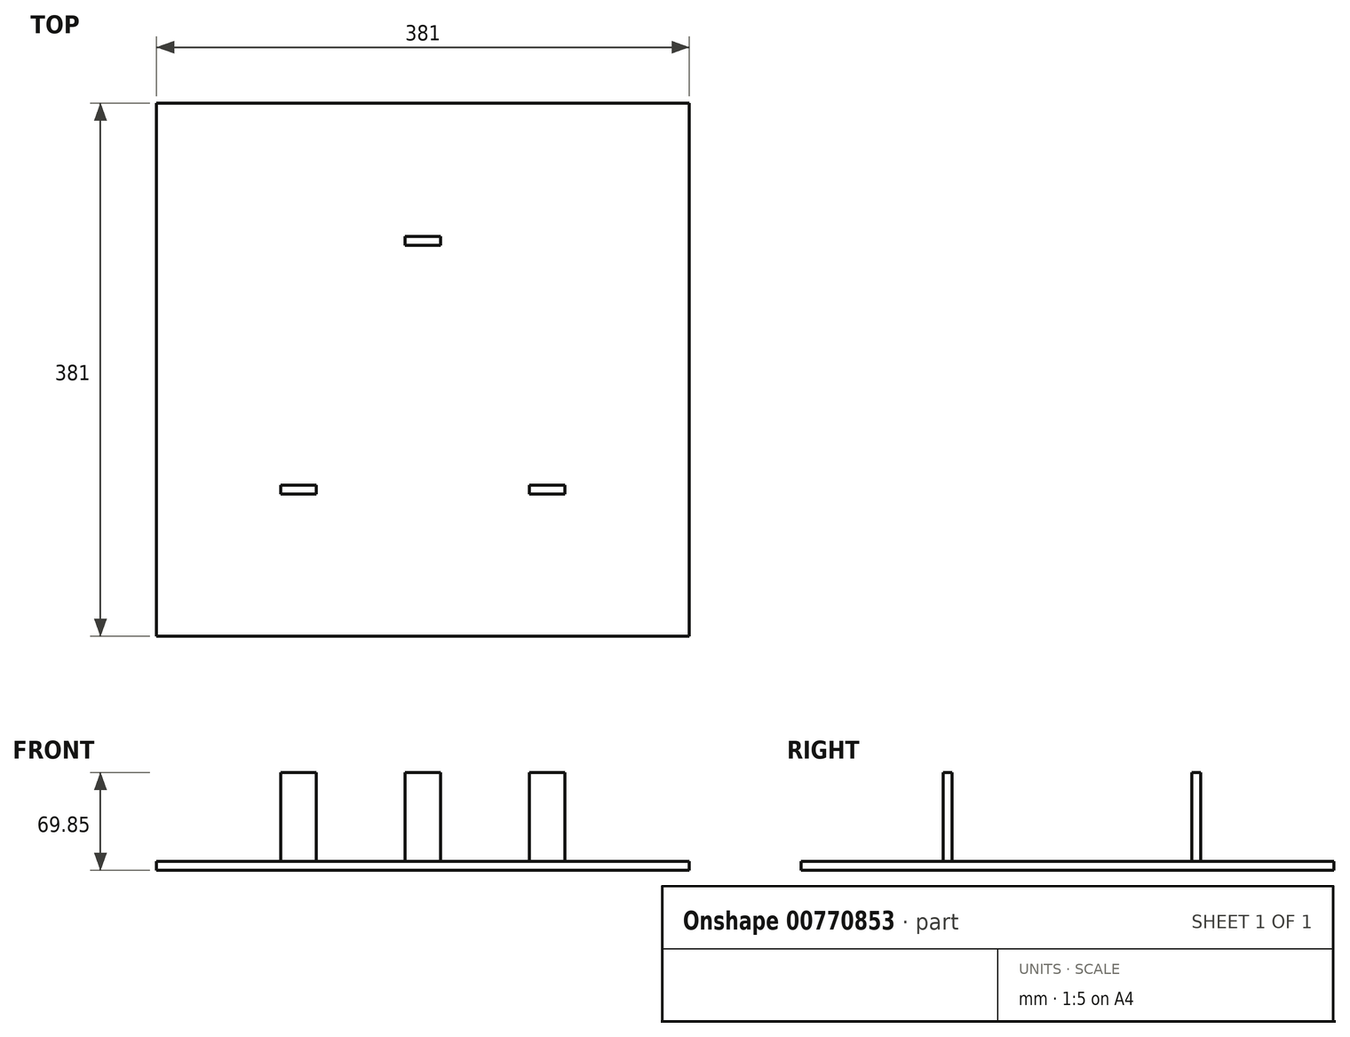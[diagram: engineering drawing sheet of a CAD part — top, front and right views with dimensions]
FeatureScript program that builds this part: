
annotation { "Feature Type Name" : "Feature", "Feature Type Description" : "" }
export const myFeature = defineFeature(function(context is Context, id is Id, definition is map)
    precondition{}
    {
        {
            var Q0;
            Q0=qCreatedBy(makeId("Top.planeOp"),FACE);
            var sketch = newSketch(context, id + "F0", { "sketchPlane" : qUnion([Q0])});
            skLineSegment(sketch, "E0.bottom", {"start": v(-202.72, 255.29) * mm, "end": v(178.28, 255.29) * mm});
            skLineSegment(sketch, "E0.top", {"start": v(-202.72, -125.71) * mm, "end": v(178.28, -125.71) * mm});
            skLineSegment(sketch, "E0.left", {"start": v(-202.72, 255.29) * mm, "end": v(-202.72, -125.71) * mm});
            skLineSegment(sketch, "E0.right", {"start": v(178.28, 255.29) * mm, "end": v(178.28, -125.71) * mm});
            skSolve(sketch);
        }
        {
            var Q0;
            Q0 = qSketchRegion(id + "F0", true);
            extrude(context, id + "F1", {"entities" : qUnion([Q0]), "depth" : 6.35 * mm, "offsetDistance" : 25.4 * mm});
        }
        {
            var Q0;
            Q0=makeQuery(id+"F1.opExtrude","CAP_FACE",FACE,{"disambiguationData":[OSD([sQuery(id+"F0.wireOp",EDGE,"E0.bottom"),sQuery(id+"F0.wireOp",EDGE,"E0.top"),sQuery(id+"F0.wireOp",EDGE,"E0.left"),sQuery(id+"F0.wireOp",EDGE,"E0.right")])],"isStart":false});
            var sketch = newSketch(context, id + "F2", { "sketchPlane" : qUnion([Q0])});
            skLineSegment(sketch, "E1.bottom", {"start": v(-24.92, 160.04) * mm, "end": v(0.48, 160.04) * mm});
            skLineSegment(sketch, "E1.top", {"start": v(-24.92, 153.69) * mm, "end": v(0.48, 153.69) * mm});
            skLineSegment(sketch, "E1.left", {"start": v(-24.92, 160.04) * mm, "end": v(-24.92, 153.69) * mm});
            skLineSegment(sketch, "E1.right", {"start": v(0.48, 160.04) * mm, "end": v(0.48, 153.69) * mm});
            skLineSegment(sketch, "E2.bottom", {"start": v(63.98, -17.76) * mm, "end": v(89.38, -17.76) * mm});
            skLineSegment(sketch, "E2.top", {"start": v(63.98, -24.11) * mm, "end": v(89.38, -24.11) * mm});
            skLineSegment(sketch, "E2.left", {"start": v(63.98, -17.76) * mm, "end": v(63.98, -24.11) * mm});
            skLineSegment(sketch, "E2.right", {"start": v(89.38, -17.76) * mm, "end": v(89.38, -24.11) * mm});
            skLineSegment(sketch, "E3.top", {"start": v(-113.82, -24.11) * mm, "end": v(-88.42, -24.11) * mm});
            skLineSegment(sketch, "E3.right", {"start": v(-88.42, -17.76) * mm, "end": v(-88.42, -24.11) * mm});
            skLineSegment(sketch, "E4", {"start": v(-88.42, -17.76) * mm, "end": v(-113.82, -17.76) * mm});
            skLineSegment(sketch, "E5", {"start": v(-113.82, -17.76) * mm, "end": v(-113.82, -24.11) * mm});
            skSolve(sketch);
        }
        {
            var Q0;
            Q0 = qSketchRegion(id + "F2", true);
            extrude(context, id + "F3", {"entities" : qUnion([Q0]), "operationType" : NewBodyOperationType.ADD, "depth" : 63.5 * mm, "offsetDistance" : 25.4 * mm});
        }
    });
